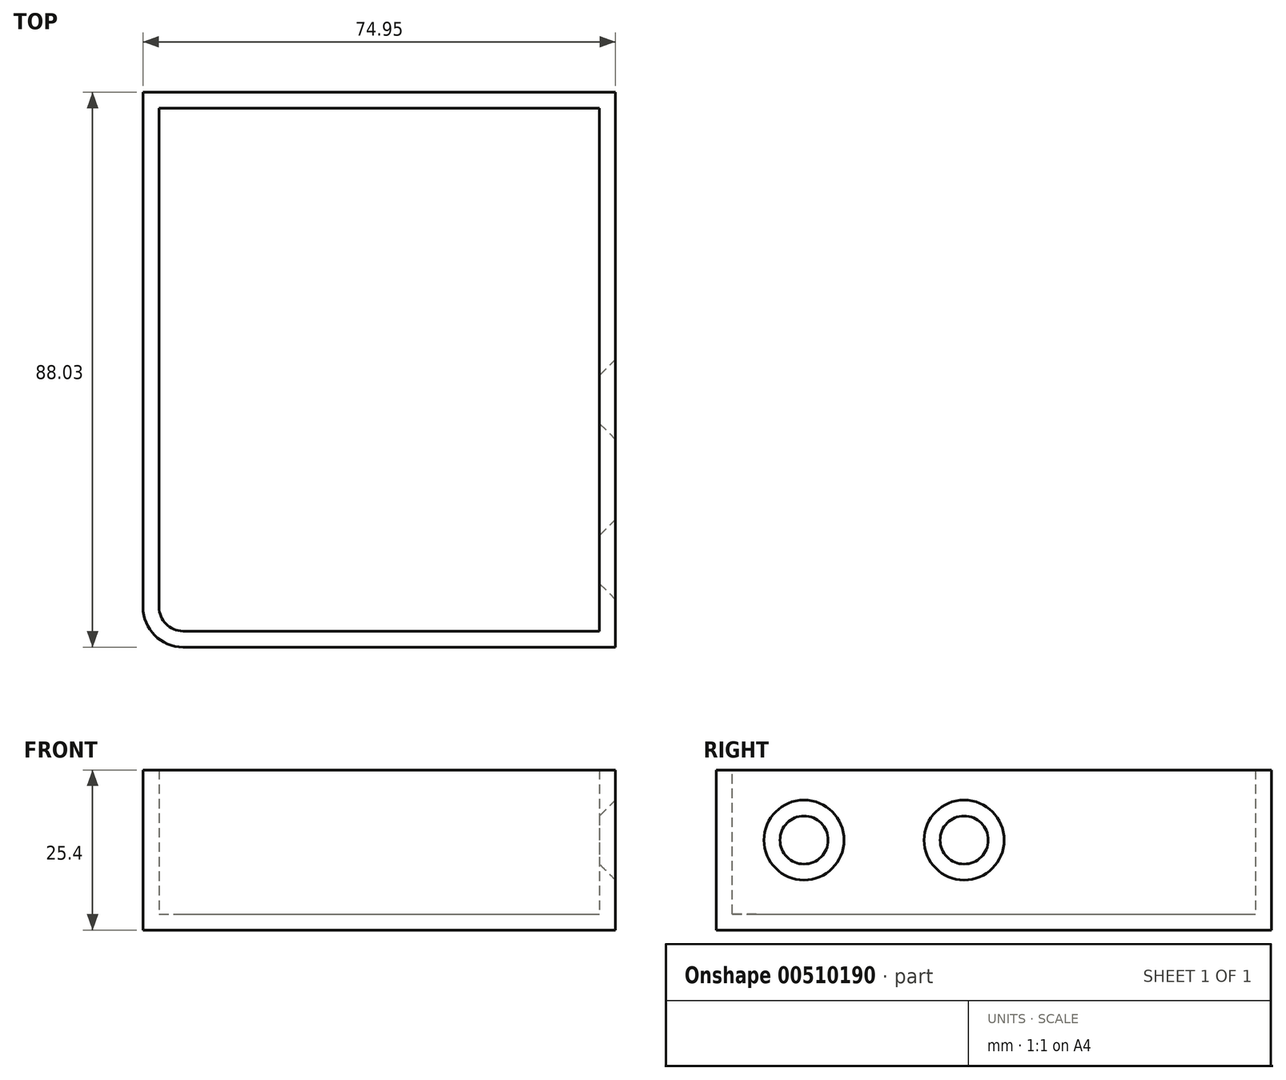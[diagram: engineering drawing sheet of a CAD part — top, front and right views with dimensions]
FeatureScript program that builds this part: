
annotation { "Feature Type Name" : "Feature", "Feature Type Description" : "" }
export const myFeature = defineFeature(function(context is Context, id is Id, definition is map)
    precondition{}
    {
        {
            var Q0;
            Q0=qCreatedBy(makeId("Top.planeOp"),FACE);
            var sketch = newSketch(context, id + "F0", { "sketchPlane" : qUnion([Q0])});
            skLineSegment(sketch, "E0.bottom", {"start": v(-50.7, -60.05) * mm, "end": v(17.89, -60.05) * mm});
            skLineSegment(sketch, "E0.top", {"start": v(-57.06, 27.98) * mm, "end": v(17.89, 27.98) * mm});
            skLineSegment(sketch, "E0.left", {"start": v(-57.06, -53.7) * mm, "end": v(-57.06, 27.98) * mm});
            skLineSegment(sketch, "E0.right", {"start": v(17.89, -60.05) * mm, "end": v(17.89, 27.98) * mm});
            skPoint(sketch, "E1.visualSharp", {"position": v(-57.06, -60.05) * mm});
            skArc(sketch, "E1.filletArc", {"start": v(-57.06, -53.7) * mm, "mid": v(-55.2, -58.2) * mm, "end": v(-50.7, -60.05) * mm});
            skSolve(sketch);
        }
        {
            var Q0;
            Q0=makeQuery(id+"F0.imprint","IMPRINT",FACE,{"disambiguationData":[TD([[makeQuery(id+"F0.imprint","IMPRINT",EDGE,{"derivedFrom":sQuery(id+"F0.wireOp",EDGE,"E0.bottom")}),1.0]])]});
            extrude(context, id + "F1", {"entities" : qUnion([Q0]), "depth" : 25.4 * mm});
        }
        {
            var Q0;
            Q0=makeQuery(id+"F1.opExtrude","CAP_FACE",FACE,{"disambiguationData":[OSD([sQuery(id+"F0.wireOp",EDGE,"E0.bottom"),sQuery(id+"F0.wireOp",EDGE,"E0.top"),sQuery(id+"F0.wireOp",EDGE,"E0.left"),sQuery(id+"F0.wireOp",EDGE,"E0.right"),sQuery(id+"F0.wireOp",EDGE,"E1.filletArc")])],"isStart":false});
            shell(context, id + "F2", {"entities" : qUnion([Q0]), "thickness" : 2.54 * mm});
        }
        {
            var Q0;
            Q0=makeQuery(id+"F1.opExtrude","SWEPT_FACE",FACE,{"disambiguationData":[OSD([sQuery(id+"F0.wireOp",EDGE,"E0.right")])]});
            var sketch = newSketch(context, id + "F3", { "sketchPlane" : qUnion([Q0])});
            skPoint(sketch, "E2", {"position": v(-46.14, 14.27) * mm});
            skPoint(sketch, "E3", {"position": v(-20.74, 14.27) * mm});
            skSolve(sketch);
        }
        {
            var Q0;
            Q0=sQuery(id+"F3.wireOp",VERTEX,"E2");
            var Q1;
            Q1=sQuery(id+"F3.wireOp",VERTEX,"E3");
            var Q2;
            Q2=makeQuery(id+"F1.opExtrude","SWEPT_BODY",BODY,{"disambiguationData":[OSD([sQuery(id+"F0.wireOp",EDGE,"E0.bottom"),sQuery(id+"F0.wireOp",EDGE,"E0.top"),sQuery(id+"F0.wireOp",EDGE,"E0.left"),sQuery(id+"F0.wireOp",EDGE,"E0.right"),sQuery(id+"F0.wireOp",EDGE,"E1.filletArc")])]});
            hole(context, id + "F4", {"style" : HoleStyle.C_SINK, "endStyle" : HoleEndStyle.BLIND, "holeDiameter" : 6.35 * mm, "cSinkDiameter" : 12.7 * mm, "cSinkAngle" : 90 * degree, "holeDepth" : 12.7 * mm, "isTappedThrough" : true, "tappedDepth" : 12.7 * mm, "tapClearance" : 3, "locations" : qUnion([Q0, Q1]), "scope" : qUnion([Q2])});
        }
    });
